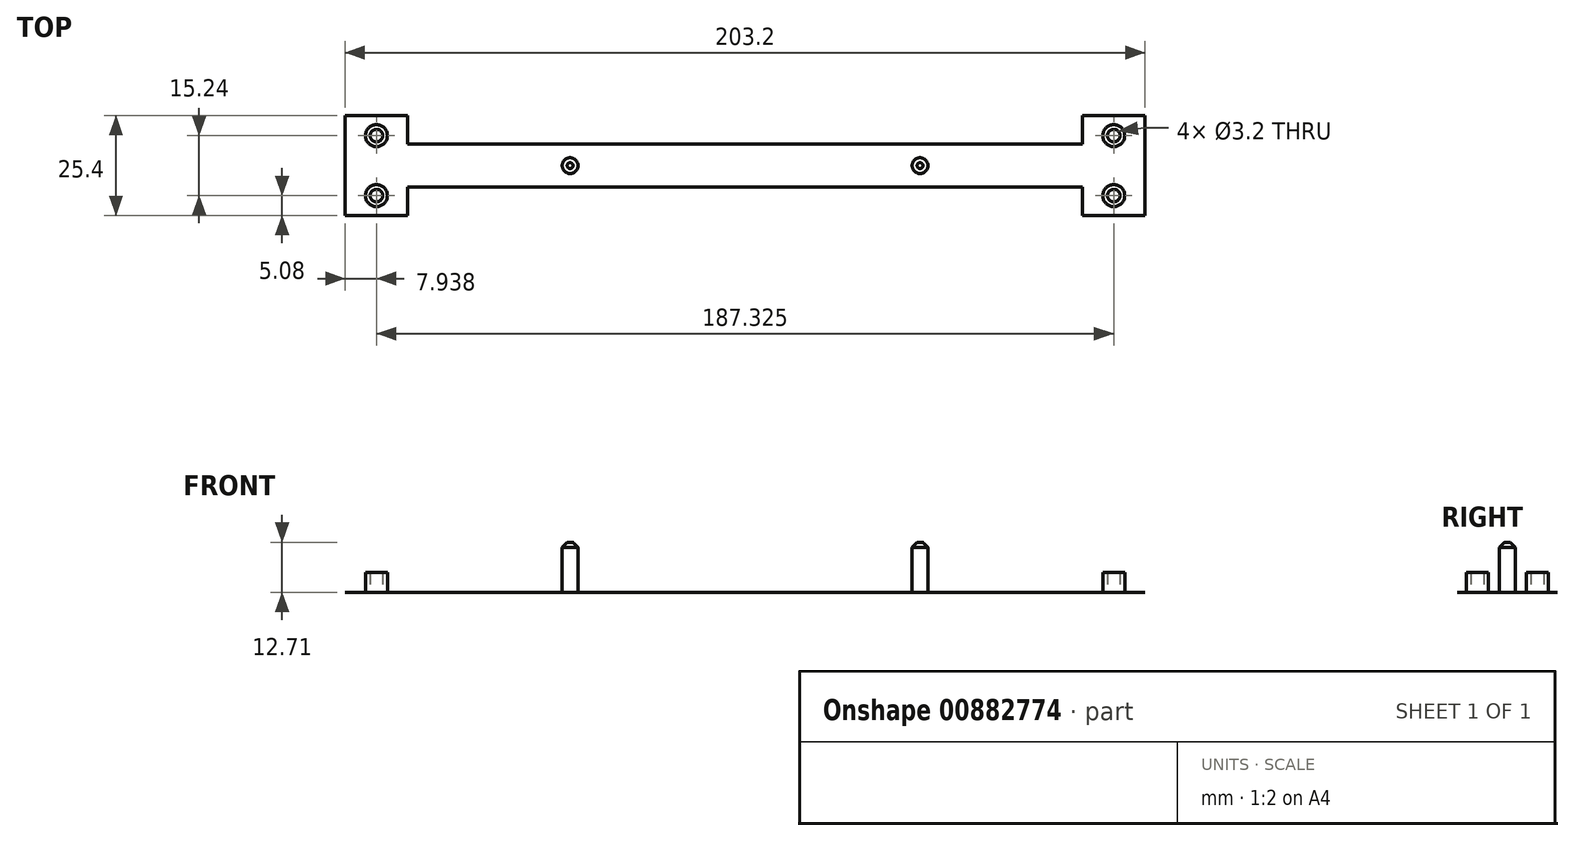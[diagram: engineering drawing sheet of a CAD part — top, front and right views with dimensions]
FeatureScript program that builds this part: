
annotation { "Feature Type Name" : "Feature", "Feature Type Description" : "" }
export const myFeature = defineFeature(function(context is Context, id is Id, definition is map)
    precondition{}
    {
        {
            var Q0;
            Q0=qCreatedBy(makeId("Top.planeOp"),FACE);
            var sketch = newSketch(context, id + "F0", { "sketchPlane" : qUnion([Q0])});
            skLineSegment(sketch, "E0.bottom", {"start": v(85.73, -5.5) * mm, "end": v(-85.73, -5.5) * mm});
            skLineSegment(sketch, "E0.top", {"start": v(85.73, 5.5) * mm, "end": v(-85.73, 5.5) * mm});
            skLineSegment(sketch, "E0.left", {"start": v(101.6, -5.5) * mm, "end": v(101.6, 5.5) * mm});
            skLineSegment(sketch, "E0.right", {"start": v(-101.6, -5.5) * mm, "end": v(-101.6, 5.5) * mm});
            skPoint(sketch, "E0.middle", {"position": v(0, 0) * mm});
            skLineSegment(sketch, "E1.bottom", {"start": v(-101.6, -12.7) * mm, "end": v(-85.73, -12.7) * mm});
            skLineSegment(sketch, "E1.top", {"start": v(-101.6, 12.7) * mm, "end": v(-85.73, 12.7) * mm});
            skLineSegment(sketch, "E1.left", {"start": v(-101.6, -12.7) * mm, "end": v(-101.6, 12.7) * mm});
            skLineSegment(sketch, "E1.right", {"start": v(-85.73, -12.7) * mm, "end": v(-85.73, -5.5) * mm});
            skLineSegment(sketch, "E2.trimOffspring", {"start": v(-85.73, 5.5) * mm, "end": v(-85.73, 12.7) * mm});
            skLineSegment(sketch, "E3.bottom", {"start": v(101.6, -12.7) * mm, "end": v(85.73, -12.7) * mm});
            skLineSegment(sketch, "E3.top", {"start": v(101.6, 12.7) * mm, "end": v(85.73, 12.7) * mm});
            skLineSegment(sketch, "E3.left", {"start": v(101.6, -12.7) * mm, "end": v(101.6, 12.7) * mm});
            skLineSegment(sketch, "E3.right", {"start": v(85.73, -12.7) * mm, "end": v(85.73, -5.5) * mm});
            skLineSegment(sketch, "E4.trimOffspring", {"start": v(85.73, 5.5) * mm, "end": v(85.73, 12.7) * mm});
            skSolve(sketch);
        }
        {
            var Q0;
            Q0 = qSketchRegion(id + "F0", true);
            extrude(context, id + "F1", {"entities" : qUnion([Q0]), "depth" : 3 / 203.2 * mm, "offsetDistance" : 25.4 * mm});
        }
        {
            var Q0;
            Q0=makeQuery(id+"F1.opExtrude","CAP_FACE",FACE,{"disambiguationData":[OSD([sQuery(id+"F0.wireOp",EDGE,"E0.bottom"),sQuery(id+"F0.wireOp",EDGE,"E0.top"),sQuery(id+"F0.wireOp",EDGE,"E1.bottom"),sQuery(id+"F0.wireOp",EDGE,"E1.top"),sQuery(id+"F0.wireOp",EDGE,"E1.left"),sQuery(id+"F0.wireOp",EDGE,"E1.right"),sQuery(id+"F0.wireOp",EDGE,"E2.trimOffspring"),sQuery(id+"F0.wireOp",EDGE,"E3.bottom"),sQuery(id+"F0.wireOp",EDGE,"E3.top"),sQuery(id+"F0.wireOp",EDGE,"E3.left"),sQuery(id+"F0.wireOp",EDGE,"E3.right"),sQuery(id+"F0.wireOp",EDGE,"E4.trimOffspring")])],"isStart":false});
            var sketch = newSketch(context, id + "F2", { "sketchPlane" : qUnion([Q0])});
            skCircle(sketch, "E5", {"center": v(-93.66, 7.62) * mm, "radius": 2.8 * mm});
            skCircle(sketch, "E6", {"center": v(-93.66, -7.62) * mm, "radius": 2.8 * mm});
            skLineSegment(sketch, "E7", {"start": v(-93.66, -12.7) * mm, "end": v(-93.66, 12.7) * mm});
            skCircle(sketch, "E8.MirrorC", {"center": v(93.66, 7.62) * mm, "radius": 2.8 * mm});
            skCircle(sketch, "E9.MirrorC", {"center": v(93.66, -7.62) * mm, "radius": 2.8 * mm});
            skSolve(sketch);
        }
        {
            var Q0;
            Q0 = qSketchRegion(id + "F2", true);
            extrude(context, id + "F3", {"entities" : qUnion([Q0]), "operationType" : NewBodyOperationType.REMOVE, "endBound" : BoundingType.UP_TO_NEXT, "oppositeDirection" : true, "depth" : 25.4 * mm, "offsetDistance" : 25.4 * mm});
        }
        {
            var Q0;
            Q0=makeQuery(id+"F2.imprint","IMPRINT",FACE,{"disambiguationData":[TD([[makeQuery(id+"F2.imprint","IMPRINT",EDGE,{"derivedFrom":sQuery(id+"F2.wireOp",EDGE,"E8.MirrorC")}),1.0]])]});
            var sketch = newSketch(context, id + "F4", { "sketchPlane" : qUnion([Q0])});
            skCircle(sketch, "E10", {"center": v(-44.45, 0) * mm, "radius": 2 * mm});
            skCircle(sketch, "E11.MirrorC", {"center": v(44.45, 0) * mm, "radius": 2 * mm});
            skSolve(sketch);
        }
        {
            var Q0;
            Q0 = qSketchRegion(id + "F4", true);
            extrude(context, id + "F5", {"entities" : qUnion([Q0]), "operationType" : NewBodyOperationType.ADD, "depth" : 12.7 * mm, "offsetDistance" : 25.4 * mm});
        }
        {
            var Q0;
            Q0=makeQuery(id+"F5.opExtrude","CAP_EDGE",EDGE,{"disambiguationData":[OSD([sQuery(id+"F4.wireOp",EDGE,"E10")])],"isStart":false});
            var Q1;
            Q1=makeQuery(id+"F5.opExtrude","CAP_EDGE",EDGE,{"disambiguationData":[OSD([sQuery(id+"F4.wireOp",EDGE,"E11.MirrorC")])],"isStart":false});
            chamfer(context, id + "F6", {"entities" : qUnion([Q0, Q1]), "width" : 1.27 * mm, "tangentPropagation" : true});
        }
        {
            var Q0;
            Q0=makeQuery(id+"F1.opExtrude","CAP_EDGE",EDGE,{"disambiguationData":[OSD([sQuery(id+"F0.wireOp",EDGE,"E1.left")])],"isStart":false});
            var Q1;
            Q1=makeQuery(id+"F1.opExtrude","CAP_EDGE",EDGE,{"disambiguationData":[OSD([sQuery(id+"F0.wireOp",EDGE,"E3.left")])],"isStart":false});
            fillet(context, id + "F7", {"entities" : qUnion([Q0, Q1]), "radius" : 5.08 * mm, "tangentPropagation" : true, "allowEdgeOverflow" : false});
        }
        {
            var Q0;
            Q0=makeQuery(id+"F1.opExtrude","CAP_FACE",FACE,{"disambiguationData":[OSD([sQuery(id+"F0.wireOp",EDGE,"E0.bottom"),sQuery(id+"F0.wireOp",EDGE,"E0.top"),sQuery(id+"F0.wireOp",EDGE,"E1.bottom"),sQuery(id+"F0.wireOp",EDGE,"E1.top"),sQuery(id+"F0.wireOp",EDGE,"E1.left"),sQuery(id+"F0.wireOp",EDGE,"E1.right"),sQuery(id+"F0.wireOp",EDGE,"E2.trimOffspring"),sQuery(id+"F0.wireOp",EDGE,"E3.bottom"),sQuery(id+"F0.wireOp",EDGE,"E3.top"),sQuery(id+"F0.wireOp",EDGE,"E3.left"),sQuery(id+"F0.wireOp",EDGE,"E3.right"),sQuery(id+"F0.wireOp",EDGE,"E4.trimOffspring")])],"isStart":true});
            var sketch = newSketch(context, id + "F8", { "sketchPlane" : qUnion([Q0])});
            skCircle(sketch, "E12", {"center": v(93.66, 7.62) * mm, "radius": 2.8 * mm});
            skCircle(sketch, "E13", {"center": v(93.66, 7.62) * mm, "radius": 1.6 * mm});
            skCircle(sketch, "E14", {"center": v(93.66, -7.62) * mm, "radius": 2.8 * mm});
            skCircle(sketch, "E15", {"center": v(93.66, -7.62) * mm, "radius": 1.6 * mm});
            skCircle(sketch, "E16.MirrorC", {"center": v(-93.66, 7.62) * mm, "radius": 2.8 * mm});
            skCircle(sketch, "E17.MirrorC", {"center": v(-93.66, -7.62) * mm, "radius": 2.8 * mm});
            skCircle(sketch, "E18.MirrorC", {"center": v(-93.66, -7.62) * mm, "radius": 1.6 * mm});
            skCircle(sketch, "E19.MirrorC", {"center": v(-93.66, 7.62) * mm, "radius": 1.6 * mm});
            skSolve(sketch);
        }
        {
            var Q0;
            Q0 = qSketchRegion(id + "F8", true);
            extrude(context, id + "F9", {"entities" : qUnion([Q0]), "operationType" : NewBodyOperationType.ADD, "oppositeDirection" : true, "depth" : 5 * mm, "offsetDistance" : 25.4 * mm});
        }
    });
